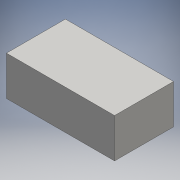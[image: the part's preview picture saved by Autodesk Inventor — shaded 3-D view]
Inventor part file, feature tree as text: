
AUTODESK INVENTOR PART (.ipt)
format: ipt  version: 2016 (Build 200138000, 138)  size: 84,992 bytes
history: native  units: mm
features: extrude x1, sketch x1
ambient origin geometry x8: Origin, YZ Plane, XZ Plane, XY Plane, X Axis, Y Axis, Z Axis, Center Point
bodies: Solid1 (feature_tree)
feature tree (2):
  extrude  "Extrusion1"  Depth=18.0mm
  sketch  "Sketch1"  dims[d0=33.0mm d1=18.0mm d2=12.0mm d3=0.0mm]
